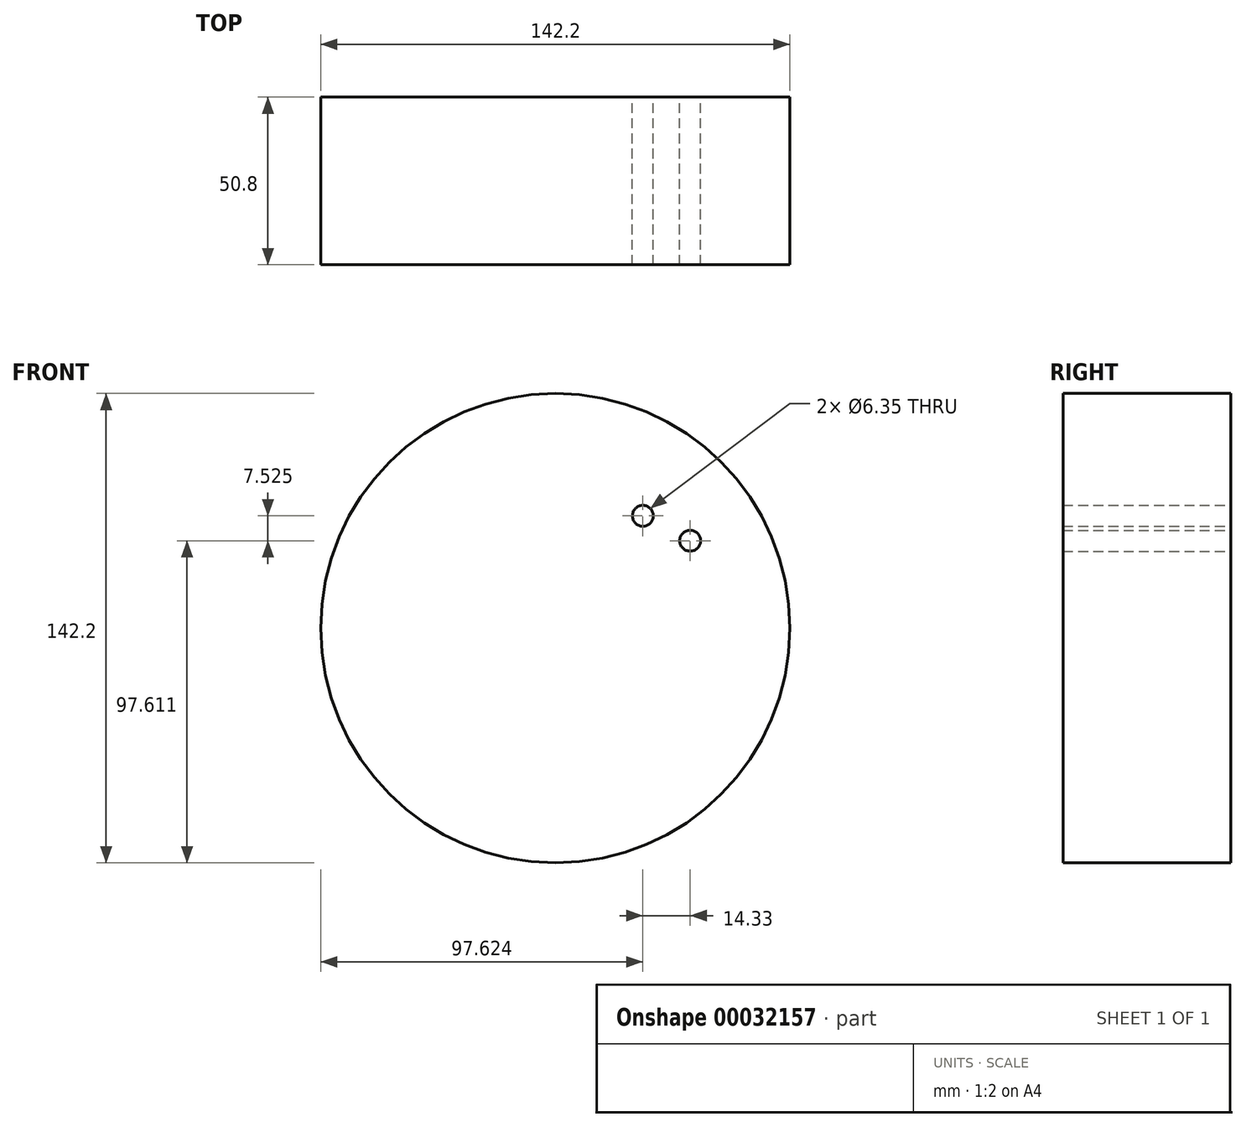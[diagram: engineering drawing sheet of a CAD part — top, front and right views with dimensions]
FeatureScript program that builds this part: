
annotation { "Feature Type Name" : "Feature", "Feature Type Description" : "" }
export const myFeature = defineFeature(function(context is Context, id is Id, definition is map)
    precondition{}
    {
        {
            var Q0;
            Q0=qCreatedBy(makeId("Front.planeOp"),FACE);
            var sketch = newSketch(context, id + "F0", { "sketchPlane" : qUnion([Q0])});
            skCircle(sketch, "E0", {"center": v(0, 0) * mm, "radius": 71.1 * mm});
            skSolve(sketch);
        }
        {
            var Q0;
            Q0 = qSketchRegion(id + "F0", true);
            extrude(context, id + "F1", {"entities" : qUnion([Q0]), "depth" : 50.8 * mm});
        }
        {
            var Q0;
            Q0=makeQuery(id+"F1.opExtrude","CAP_FACE",FACE,{"disambiguationData":[OSD([sQuery(id+"F0.wireOp",EDGE,"E0")])],"isStart":true});
            var sketch = newSketch(context, id + "F2", { "sketchPlane" : qUnion([Q0])});
            skCircle(sketch, "E1.cCircle", {"center": v(-23.35, 10.59) * mm, "radius": 22.23 * mm, "construction": true});
            skLineSegment(sketch, "E1.0", {"start": v(-28.39, -12.53) * mm, "end": v(-42.07, -3.88) * mm});
            skLineSegment(sketch, "E1.1", {"start": v(-42.07, -3.88) * mm, "end": v(-47, 11.54) * mm});
            skLineSegment(sketch, "E1.2", {"start": v(-47, 11.54) * mm, "end": v(-40.85, 26.51) * mm});
            skLineSegment(sketch, "E1.3", {"start": v(-40.85, 26.51) * mm, "end": v(-26.52, 34.04) * mm});
            skLineSegment(sketch, "E1.4", {"start": v(-26.52, 34.04) * mm, "end": v(-10.7, 30.59) * mm});
            skLineSegment(sketch, "E1.5", {"start": v(-10.7, 30.59) * mm, "end": v(-0.81, 17.78) * mm});
            skLineSegment(sketch, "E1.6", {"start": v(-0.81, 17.78) * mm, "end": v(-1.46, 1.61) * mm});
            skLineSegment(sketch, "E1.7", {"start": v(-1.46, 1.61) * mm, "end": v(-12.35, -10.36) * mm});
            skLineSegment(sketch, "E1.8", {"start": v(-12.35, -10.36) * mm, "end": v(-28.39, -12.53) * mm});
            skPoint(sketch, "E1.0.midPoint", {"position": v(-35.23, -8.2) * mm});
            skSolve(sketch);
        }
        {
            var Q0;
            Q0=sQuery(id+"F2.wireOp",VERTEX,"E1.3.start");
            var Q1;
            Q1=sQuery(id+"F2.wireOp",VERTEX,"E1.4.start");
            var Q2;
            Q2=makeQuery(id+"F1.opExtrude","SWEPT_BODY",BODY,{"disambiguationData":[OSD([sQuery(id+"F0.wireOp",EDGE,"E0")])]});
            hole(context, id + "F3", {"style" : HoleStyle.SIMPLE, "holeDiameter" : 6.35 * mm, "endStyle" : HoleEndStyle.THROUGH, "locations" : qUnion([Q0, Q1]), "scope" : qUnion([Q2])});
        }
    });
